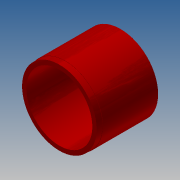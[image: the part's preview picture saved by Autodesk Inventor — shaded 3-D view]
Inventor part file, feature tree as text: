
AUTODESK INVENTOR PART (.ipt)
format: ipt  version: 2017.3 (Build 213257000, 257)  size: 169,984 bytes
history: native  units: in
note: dims shown in document units (in); Inventor stores cm internally (conversion verified against a paired STEP export)
features: extrude x2, sketch x2, fillet x1, chamfer x1
ambient origin geometry x8: Origin, YZ Plane, XZ Plane, XY Plane, X Axis, Y Axis, Z Axis, Center Point
bodies: Solid1 (feature_tree)
feature tree (6):
  extrude  "Extrusion1"  Depth=12.73in
  extrude  "Extrusion2"  Depth=0.0312in
  fillet  "Fillet1"  Radius=1.0in
  chamfer  "Chamfer1"  Distance=0.0312in
  sketch  "Sketch1"  dims[d0=11.1417in d1=12.73in]
  sketch  "Sketch2"  dims[d2=10.3543in d3=0.0in d4=12.605in d5=1.0in d6=0.0in d10=0.0312in d11=0.0312in d12=0.125in d13=45.0deg]
